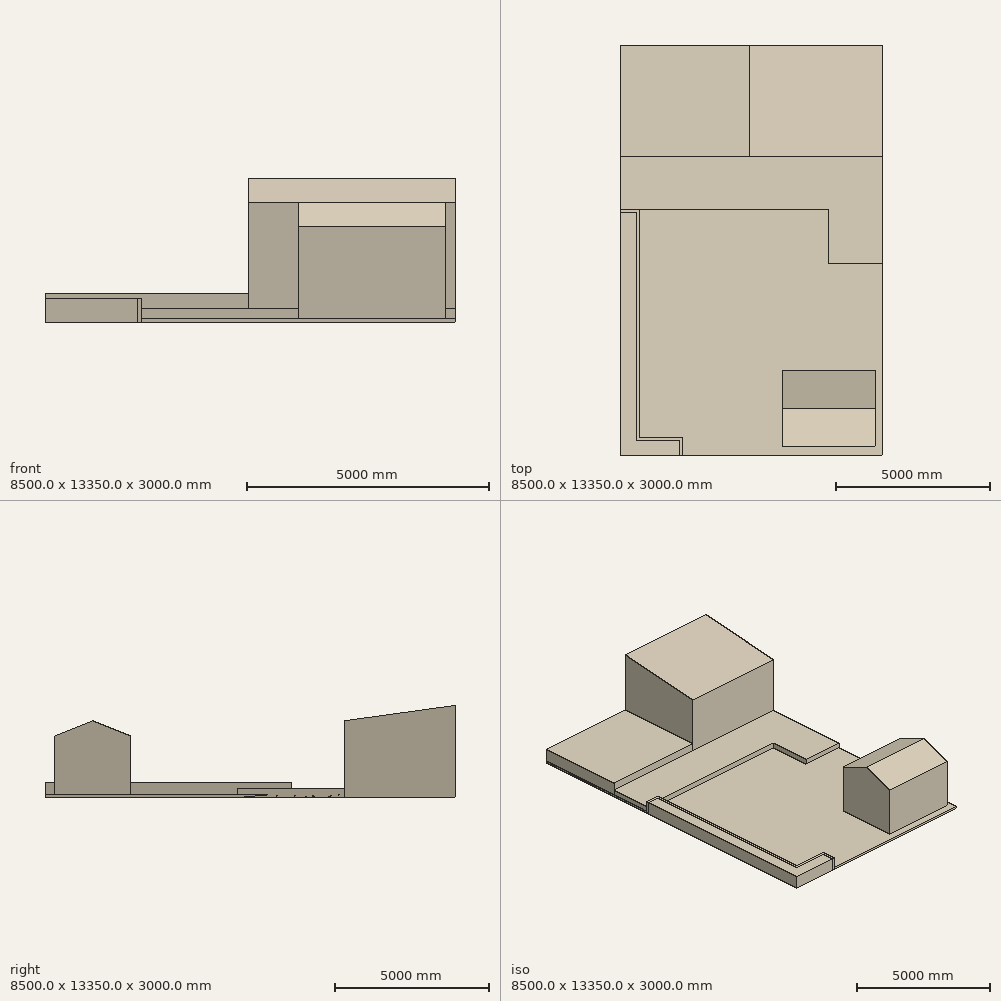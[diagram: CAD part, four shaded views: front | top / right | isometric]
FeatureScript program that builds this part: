
annotation { "Feature Type Name" : "Feature", "Feature Type Description" : "" }
export const myFeature = defineFeature(function(context is Context, id is Id, definition is map)
    precondition{}
    {
        {
            var Q0;
            Q0=qCreatedBy(makeId("Top.planeOp"),FACE);
            var sketch = newSketch(context, id + "F0", { "sketchPlane" : qUnion([Q0])});
            skLineSegment(sketch, "E0.bottom", {"start": v(4250, 0) * mm, "end": v(-4250, 0) * mm});
            skLineSegment(sketch, "E0.top", {"start": v(4250, -8000) * mm, "end": v(-4250, -8000) * mm});
            skLineSegment(sketch, "E0.left", {"start": v(4250, 0) * mm, "end": v(4250, -8000) * mm});
            skLineSegment(sketch, "E0.right", {"start": v(-4250, 0) * mm, "end": v(-4250, -8000) * mm});
            skLineSegment(sketch, "E1.bottom", {"start": v(-4250, 0) * mm, "end": v(4250, 0) * mm});
            skLineSegment(sketch, "E1.top", {"start": v(-4250, 1750) * mm, "end": v(4250, 1750) * mm});
            skLineSegment(sketch, "E1.left", {"start": v(-4250, 0) * mm, "end": v(-4250, 1750) * mm});
            skLineSegment(sketch, "E1.right", {"start": v(4250, 0) * mm, "end": v(4250, 1750) * mm});
            skLineSegment(sketch, "E2.bottom", {"start": v(2500, 0) * mm, "end": v(4250, 0) * mm});
            skLineSegment(sketch, "E2.top", {"start": v(2500, -1750) * mm, "end": v(4250, -1750) * mm});
            skLineSegment(sketch, "E2.left", {"start": v(2500, 0) * mm, "end": v(2500, -1750) * mm});
            skLineSegment(sketch, "E2.right", {"start": v(4250, 0) * mm, "end": v(4250, -1750) * mm});
            skLineSegment(sketch, "E3.bottom", {"start": v(-4250, 1750) * mm, "end": v(-50, 1750) * mm});
            skLineSegment(sketch, "E3.top", {"start": v(-4250, 5350) * mm, "end": v(-50, 5350) * mm});
            skLineSegment(sketch, "E3.left", {"start": v(-4250, 1750) * mm, "end": v(-4250, 5350) * mm});
            skLineSegment(sketch, "E3.right", {"start": v(-50, 1750) * mm, "end": v(-50, 5350) * mm});
            skLineSegment(sketch, "E4", {"start": v(-3650, 0) * mm, "end": v(-3650, -7400) * mm});
            skLineSegment(sketch, "E5", {"start": v(-3650, -7400) * mm, "end": v(-2250, -7400) * mm});
            skLineSegment(sketch, "E6", {"start": v(-2250, -7400) * mm, "end": v(-2250, -8000) * mm});
            skLineSegment(sketch, "E7.bottom", {"start": v(4050, -7700) * mm, "end": v(1000, -7700) * mm});
            skLineSegment(sketch, "E7.top", {"start": v(4050, -5217) * mm, "end": v(1000, -5217) * mm});
            skLineSegment(sketch, "E7.left", {"start": v(4050, -7700) * mm, "end": v(4050, -5217) * mm});
            skLineSegment(sketch, "E7.right", {"start": v(1000, -7700) * mm, "end": v(1000, -5217) * mm});
            skLineSegment(sketch, "E8.0", {"start": v(-2350, -7500) * mm, "end": v(-2350, -8000) * mm});
            skLineSegment(sketch, "E8.1", {"start": v(-3750, -7500) * mm, "end": v(-2350, -7500) * mm});
            skLineSegment(sketch, "E8.2", {"start": v(-3750, 0) * mm, "end": v(-3750, -7500) * mm});
            skLineSegment(sketch, "E9", {"start": v(-3650, -100) * mm, "end": v(-4250, -100) * mm});
            skLineSegment(sketch, "E10", {"start": v(-50, 5350) * mm, "end": v(4250, 5350) * mm});
            skLineSegment(sketch, "E11", {"start": v(4250, 5350) * mm, "end": v(4250, 1750) * mm});
            skSolve(sketch);
        }
        {
            var Q0;
            {var subQ7=sQuery(id+"F0.wireOp",EDGE,"E2.top");Q0=makeQuery(id+"F0.imprint","IMPRINT",FACE,{"disambiguationData":[TD([[makeQuery(id+"F0.imprint","IMPRINT",EDGE,{"derivedFrom":subQ7}),-1.0]])]});}
            var Q1;
            Q1=makeQuery(id+"F0.imprint","IMPRINT",FACE,{"disambiguationData":[TD([[makeQuery(id+"F0.imprint","IMPRINT",EDGE,{"derivedFrom":sQuery(id+"F0.wireOp",EDGE,"E7.bottom")}),-1.0]])]});
            var Q2;
            {var subQ0=sQuery(id+"F0.wireOp",EDGE,"E8.2");var subQ1=sQuery(id+"F0.wireOp",EDGE,"E0.bottom");var subQ2=makeQuery(id+"F0.imprint","INTERSECT",VERTEX,{"derivedFrom":[subQ1,subQ0]});Q2=makeQuery(id+"F0.imprint","IMPRINT",FACE,{"disambiguationData":[TD([[makeQuery(id+"F0.imprint","IMPRINT",EDGE,{"disambiguationData":[TD([[subQ2,-1.0]])],"derivedFrom":subQ0}),-1.0]])]});}
            var Q3;
            {var subQ4=sQuery(id+"F0.wireOp",EDGE,"E2.top");Q3=makeQuery(id+"F0.imprint","IMPRINT",FACE,{"disambiguationData":[TD([[makeQuery(id+"F0.imprint","IMPRINT",EDGE,{"derivedFrom":subQ4}),1.0]])]});}
            var Q4;
            {var subQ4=sQuery(id+"F0.wireOp",EDGE,"E1.left");Q4=makeQuery(id+"F0.imprint","IMPRINT",FACE,{"disambiguationData":[TD([[makeQuery(id+"F0.imprint","IMPRINT",EDGE,{"derivedFrom":subQ4}),-1.0]])]});}
            var Q5;
            Q5=makeQuery(id+"F0.imprint","IMPRINT",FACE,{"disambiguationData":[TD([[makeQuery(id+"F0.imprint","IMPRINT",EDGE,{"derivedFrom":sQuery(id+"F0.wireOp",EDGE,"E3.top")}),-1.0]])]});
            extrude(context, id + "F1", {"entities" : qUnion([Q0, Q1, Q2, Q3, Q4, Q5]), "depth" : 100 * mm, "offsetDistance" : 25 * mm});
        }
        {
            var Q0;
            {var subQ0=sQuery(id+"F0.wireOp",EDGE,"E8.0");Q0=makeQuery(id+"F0.imprint","IMPRINT",FACE,{"disambiguationData":[TD([[makeQuery(id+"F0.imprint","IMPRINT",EDGE,{"derivedFrom":subQ0}),-1.0]])]});}
            extrude(context, id + "F2", {"entities" : qUnion([Q0]), "depth" : 500 * mm, "offsetDistance" : 25 * mm});
        }
        {
            var Q0;
            {var subQ4=sQuery(id+"F0.wireOp",EDGE,"E1.left");Q0=makeQuery(id+"F0.imprint","IMPRINT",FACE,{"disambiguationData":[TD([[makeQuery(id+"F0.imprint","IMPRINT",EDGE,{"derivedFrom":subQ4}),-1.0]])]});}
            var Q1;
            {var subQ4=sQuery(id+"F0.wireOp",EDGE,"E2.top");Q1=makeQuery(id+"F0.imprint","IMPRINT",FACE,{"disambiguationData":[TD([[makeQuery(id+"F0.imprint","IMPRINT",EDGE,{"derivedFrom":subQ4}),1.0]])]});}
            extrude(context, id + "F3", {"entities" : qUnion([Q0, Q1]), "depth" : 300 * mm, "offsetDistance" : 25 * mm});
        }
        {
            var Q0;
            Q0=makeQuery(id+"F0.imprint","IMPRINT",FACE,{"disambiguationData":[TD([[makeQuery(id+"F0.imprint","IMPRINT",EDGE,{"derivedFrom":sQuery(id+"F0.wireOp",EDGE,"E3.top")}),-1.0]])]});
            extrude(context, id + "F4", {"entities" : qUnion([Q0]), "depth" : 600 * mm, "offsetDistance" : 25 * mm});
        }
        {
            var Q0;
            Q0=makeQuery(id+"F0.imprint","IMPRINT",FACE,{"disambiguationData":[TD([[makeQuery(id+"F0.imprint","IMPRINT",EDGE,{"derivedFrom":sQuery(id+"F0.wireOp",EDGE,"E7.bottom")}),-1.0]])]});
            extrude(context, id + "F5", {"entities" : qUnion([Q0]), "depth" : 2500 * mm, "offsetDistance" : 25 * mm});
        }
        {
            var Q0;
            Q0=makeQuery(id+"F5.opExtrude","CAP_EDGE",EDGE,{"disambiguationData":[OSD([sQuery(id+"F0.wireOp",EDGE,"E7.bottom")])],"isStart":false});
            var Q1;
            Q1=makeQuery(id+"F5.opExtrude","CAP_EDGE",EDGE,{"disambiguationData":[OSD([sQuery(id+"F0.wireOp",EDGE,"E7.top")])],"isStart":false});
            chamfer(context, id + "F6", {"entities" : qUnion([Q0, Q1]), "chamferType" : ChamferType.TWO_OFFSETS, "width1" : 500 * mm, "oppositeDirection" : false, "width2" : 1250 * mm, "tangentPropagation" : true});
        }
        {
            var Q0;
            {var subQ0=sQuery(id+"F0.wireOp",EDGE,"E8.2");var subQ1=sQuery(id+"F0.wireOp",EDGE,"E0.bottom");var subQ2=makeQuery(id+"F0.imprint","INTERSECT",VERTEX,{"derivedFrom":[subQ1,subQ0]});Q0=makeQuery(id+"F0.imprint","IMPRINT",FACE,{"disambiguationData":[TD([[makeQuery(id+"F0.imprint","IMPRINT",EDGE,{"disambiguationData":[TD([[subQ2,1.0]])],"derivedFrom":subQ1}),1.0]])]});}
            var Q1;
            {var subQ1=sQuery(id+"F0.wireOp",EDGE,"E5");Q1=makeQuery(id+"F0.imprint","IMPRINT",FACE,{"disambiguationData":[TD([[makeQuery(id+"F0.imprint","IMPRINT",EDGE,{"derivedFrom":subQ1}),-1.0]])]});}
            var Q2;
            {var subQ0=sQuery(id+"F0.wireOp",EDGE,"E8.2");var subQ1=sQuery(id+"F0.wireOp",EDGE,"E0.bottom");var subQ2=makeQuery(id+"F0.imprint","INTERSECT",VERTEX,{"derivedFrom":[subQ1,subQ0]});Q2=makeQuery(id+"F0.imprint","IMPRINT",FACE,{"disambiguationData":[TD([[makeQuery(id+"F0.imprint","IMPRINT",EDGE,{"disambiguationData":[TD([[subQ2,-1.0]])],"derivedFrom":subQ0}),-1.0]])]});}
            var Q3;
            Q3=makeQuery(id+"F2.opExtrude","CAP_FACE",FACE,{"disambiguationData":[OSD([sQuery(id+"F0.wireOp",EDGE,"E0.top"),sQuery(id+"F0.wireOp",EDGE,"E0.right"),sQuery(id+"F0.wireOp",EDGE,"E8.0"),sQuery(id+"F0.wireOp",EDGE,"E8.1"),sQuery(id+"F0.wireOp",EDGE,"E8.2"),sQuery(id+"F0.wireOp",EDGE,"E9")])],"isStart":false});
            extrude(context, id + "F7", {"entities" : qUnion([Q0, Q1, Q2]), "endBound" : BoundingType.UP_TO_SURFACE, "depth" : 520 * mm, "endBoundEntityFace" : qUnion([Q3]), "offsetDistance" : 25 * mm});
        }
        {
            var Q0;
            {var subQ0=sQuery(id+"F0.wireOp",EDGE,"E3.right");Q0=makeQuery(id+"F0.imprint","IMPRINT",FACE,{"disambiguationData":[TD([[makeQuery(id+"F0.imprint","IMPRINT",EDGE,{"derivedFrom":subQ0}),-1.0]])]});}
            extrude(context, id + "F8", {"entities" : qUnion([Q0]), "depth" : 3000 * mm, "offsetDistance" : 25 * mm});
        }
        {
            var Q0;
            Q0=makeQuery(id+"F8.opExtrude","CAP_EDGE",EDGE,{"disambiguationData":[OSD([sQuery(id+"F0.wireOp",EDGE,"E1.top")])],"isStart":false});
            chamfer(context, id + "F9", {"entities" : qUnion([Q0]), "chamferType" : ChamferType.TWO_OFFSETS, "width1" : 3600 * mm, "oppositeDirection" : false, "width2" : 500 * mm, "tangentPropagation" : true});
        }
    });
